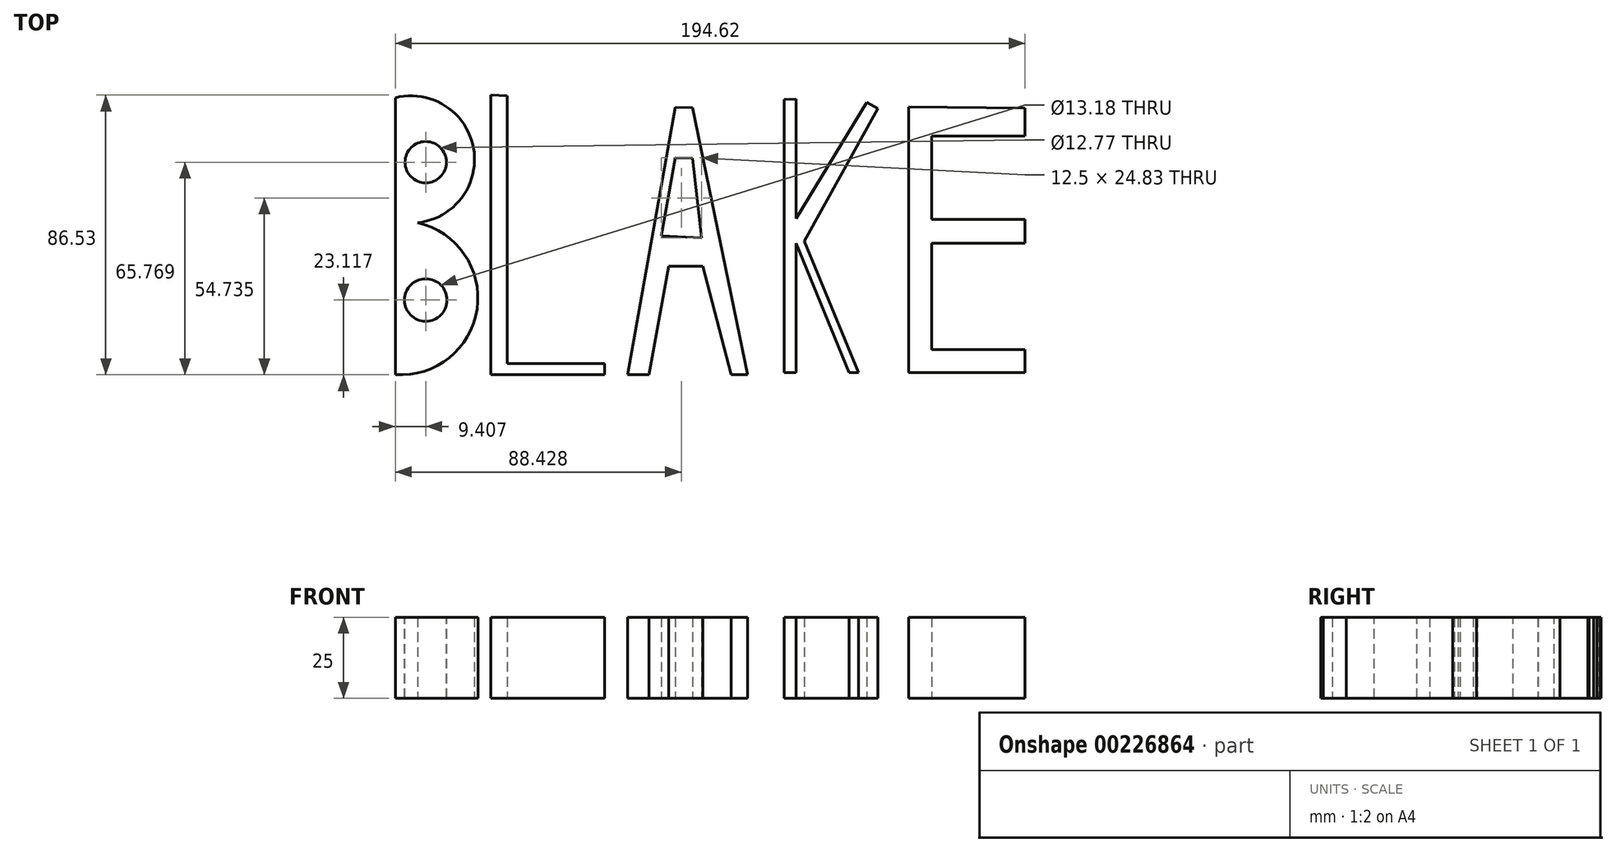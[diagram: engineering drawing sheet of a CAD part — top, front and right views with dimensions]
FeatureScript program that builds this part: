
annotation { "Feature Type Name" : "Feature", "Feature Type Description" : "" }
export const myFeature = defineFeature(function(context is Context, id is Id, definition is map)
    precondition{}
    {
        {
            var Q0;
            Q0=qCreatedBy(makeId("Top.planeOp"),FACE);
            var sketch = newSketch(context, id + "F0", { "sketchPlane" : qUnion([Q0])});
            skLineSegment(sketch, "E0", {"start": v(-86.48, 42.75) * mm, "end": v(-86.48, -42.9) * mm});
            skArc(sketch, "E1", {"start": v(-86.48, 4.57) * mm, "mid": v(-61.98, 23.66) * mm, "end": v(-86.48, 42.75) * mm});
            skArc(sketch, "E2", {"start": v(-86.48, -42.9) * mm, "mid": v(-60.94, -19.17) * mm, "end": v(-86.48, 4.57) * mm});
            skLineSegment(sketch, "E3", {"start": v(-56.92, 43.57) * mm, "end": v(-56.92, -42.88) * mm});
            skLineSegment(sketch, "E4", {"start": v(-56.92, -42.88) * mm, "end": v(-21.72, -42.88) * mm});
            skLineSegment(sketch, "E5", {"start": v(-21.72, -42.88) * mm, "end": v(-21.72, -39.43) * mm});
            skLineSegment(sketch, "E6", {"start": v(-21.72, -39.43) * mm, "end": v(-51.92, -39.43) * mm});
            skLineSegment(sketch, "E7", {"start": v(-51.92, -39.43) * mm, "end": v(-51.92, 43.4) * mm});
            skLineSegment(sketch, "E8", {"start": v(-51.92, 43.4) * mm, "end": v(-56.92, 43.57) * mm});
            skLineSegment(sketch, "E9", {"start": v(0, 39.78) * mm, "end": v(-14.7, -42.88) * mm});
            skLineSegment(sketch, "E10", {"start": v(-14.7, -42.88) * mm, "end": v(-8.02, -42.87) * mm});
            skLineSegment(sketch, "E11", {"start": v(-8.02, -42.87) * mm, "end": v(-2.03, -9.4) * mm});
            skLineSegment(sketch, "E12", {"start": v(-2.03, -9.4) * mm, "end": v(8.6, -9.4) * mm});
            skLineSegment(sketch, "E13", {"start": v(8.6, -9.4) * mm, "end": v(17.33, -42.88) * mm});
            skLineSegment(sketch, "E14", {"start": v(17.33, -42.88) * mm, "end": v(22.47, -42.88) * mm});
            skLineSegment(sketch, "E15", {"start": v(22.47, -42.88) * mm, "end": v(5.34, 39.6) * mm});
            skLineSegment(sketch, "E16", {"start": v(5.34, 39.6) * mm, "end": v(0, 39.78) * mm});
            skLineSegment(sketch, "E17", {"start": v(0, 24.19) * mm, "end": v(-4.3, 0) * mm});
            skLineSegment(sketch, "E18", {"start": v(-4.3, 0) * mm, "end": v(8.2, -0.64) * mm});
            skLineSegment(sketch, "E19", {"start": v(8.2, -0.64) * mm, "end": v(5.34, 24.02) * mm});
            skLineSegment(sketch, "E20", {"start": v(5.34, 24.02) * mm, "end": v(0, 24.19) * mm});
            skLineSegment(sketch, "E21", {"start": v(33.78, 42.18) * mm, "end": v(33.78, -42.29) * mm});
            skLineSegment(sketch, "E22", {"start": v(33.78, -42.29) * mm, "end": v(37.38, -42.29) * mm});
            skLineSegment(sketch, "E23", {"start": v(37.38, -42.29) * mm, "end": v(37.38, -2.2) * mm});
            skLineSegment(sketch, "E24", {"start": v(37.38, -2.2) * mm, "end": v(53.82, -42.29) * mm});
            skLineSegment(sketch, "E25", {"start": v(53.82, -42.29) * mm, "end": v(56.74, -42.29) * mm});
            skLineSegment(sketch, "E26", {"start": v(56.74, -42.29) * mm, "end": v(39.95, -1.68) * mm});
            skLineSegment(sketch, "E27", {"start": v(39.95, -1.68) * mm, "end": v(62.73, 39.44) * mm});
            skLineSegment(sketch, "E28", {"start": v(62.73, 39.44) * mm, "end": v(59.3, 41.34) * mm});
            skLineSegment(sketch, "E29", {"start": v(59.3, 41.34) * mm, "end": v(37.38, 5.34) * mm});
            skLineSegment(sketch, "E30", {"start": v(37.38, 5.34) * mm, "end": v(37.38, 42.35) * mm});
            skLineSegment(sketch, "E31", {"start": v(37.38, 42.35) * mm, "end": v(33.78, 42.18) * mm});
            skLineSegment(sketch, "E32", {"start": v(72.16, 39.93) * mm, "end": v(72.16, -42.29) * mm});
            skLineSegment(sketch, "E33", {"start": v(72.16, -42.29) * mm, "end": v(108.14, -42.29) * mm});
            skLineSegment(sketch, "E34", {"start": v(108.14, -42.29) * mm, "end": v(108.14, -35.1) * mm});
            skLineSegment(sketch, "E35", {"start": v(108.14, -35.1) * mm, "end": v(79.35, -35.1) * mm});
            skLineSegment(sketch, "E36", {"start": v(79.35, -35.1) * mm, "end": v(79.35, -2.21) * mm});
            skLineSegment(sketch, "E37", {"start": v(79.35, -2.21) * mm, "end": v(108.14, -2.21) * mm});
            skLineSegment(sketch, "E38", {"start": v(108.14, -2.21) * mm, "end": v(108.14, 5.15) * mm});
            skLineSegment(sketch, "E39", {"start": v(108.14, 5.15) * mm, "end": v(79.35, 5.15) * mm});
            skLineSegment(sketch, "E40", {"start": v(79.35, 5.15) * mm, "end": v(79.35, 30.85) * mm});
            skLineSegment(sketch, "E41", {"start": v(79.35, 30.85) * mm, "end": v(108.14, 30.85) * mm});
            skLineSegment(sketch, "E42", {"start": v(108.14, 30.85) * mm, "end": v(108.14, 39.59) * mm});
            skLineSegment(sketch, "E43", {"start": v(108.14, 39.59) * mm, "end": v(72.16, 39.93) * mm});
            skSolve(sketch);
        }
        {
            var Q0;
            Q0=makeQuery(id+"F0.imprint","IMPRINT",FACE,{"disambiguationData":[TD([[makeQuery(id+"F0.imprint","IMPRINT",EDGE,{"derivedFrom":sQuery(id+"F0.wireOp",EDGE,"E3")}),1.0]])]});
            var Q1;
            Q1=makeQuery(id+"F0.imprint","IMPRINT",FACE,{"disambiguationData":[TD([[makeQuery(id+"F0.imprint","IMPRINT",EDGE,{"derivedFrom":sQuery(id+"F0.wireOp",EDGE,"E21")}),1.0]])]});
            var Q2;
            Q2=makeQuery(id+"F0.imprint","IMPRINT",FACE,{"disambiguationData":[TD([[makeQuery(id+"F0.imprint","IMPRINT",EDGE,{"derivedFrom":sQuery(id+"F0.wireOp",EDGE,"E32")}),1.0]])]});
            var Q3;
            {var subQ0=sQuery(id+"F0.wireOp",EDGE,"E2");var subQ1=sQuery(id+"F0.wireOp",EDGE,"E0");var subQ2=makeQuery(id+"F0.imprint","INTERSECT",VERTEX,{"derivedFrom":[subQ1,subQ0]});Q3=makeQuery(id+"F0.imprint","IMPRINT",FACE,{"disambiguationData":[TD([[makeQuery(id+"F0.imprint","IMPRINT",EDGE,{"disambiguationData":[TD([[subQ2,-1.0]])],"derivedFrom":subQ0}),1.0]])]});}
            var Q4;
            Q4=makeQuery(id+"F0.imprint","IMPRINT",FACE,{"disambiguationData":[TD([[makeQuery(id+"F0.imprint","IMPRINT",EDGE,{"derivedFrom":sQuery(id+"F0.wireOp",EDGE,"E9")}),1.0]])]});
            var Q5;
            {var subQ0=sQuery(id+"F0.wireOp",EDGE,"E2");var subQ1=sQuery(id+"F0.wireOp",EDGE,"E1");var subQ3=makeQuery(id+"F0.imprint","INTERSECT",VERTEX,{"derivedFrom":[subQ1,subQ0]});Q5=makeQuery(id+"F0.imprint","IMPRINT",FACE,{"disambiguationData":[TD([[makeQuery(id+"F0.imprint","IMPRINT",EDGE,{"disambiguationData":[TD([[subQ3,1.0]])],"derivedFrom":subQ1}),1.0]])]});}
            var Q6;
            {var subQ0=sQuery(id+"F0.wireOp",EDGE,"E1");var subQ1=sQuery(id+"F0.wireOp",EDGE,"E0");var subQ2=makeQuery(id+"F0.imprint","INTERSECT",VERTEX,{"derivedFrom":[subQ1,subQ0]});Q6=makeQuery(id+"F0.imprint","IMPRINT",FACE,{"disambiguationData":[TD([[makeQuery(id+"F0.imprint","IMPRINT",EDGE,{"disambiguationData":[TD([[subQ2,1.0]])],"derivedFrom":subQ0}),1.0]])]});}
            extrude(context, id + "F1", {"entities" : qUnion([Q0, Q1, Q2, Q3, Q4, Q5, Q6]), "depth" : 25 * mm});
        }
        {
            var Q0;
            Q0=makeQuery(id+"F1.opExtrude","CAP_FACE",FACE,{"disambiguationData":[OSD([sQuery(id+"F0.wireOp",EDGE,"E0"),sQuery(id+"F0.wireOp",EDGE,"E1"),sQuery(id+"F0.wireOp",EDGE,"E2")])],"isStart":false});
            var sketch = newSketch(context, id + "F2", { "sketchPlane" : qUnion([Q0])});
            skCircle(sketch, "E44", {"center": v(-77.07, 22.8) * mm, "radius": 6.38 * mm});
            skCircle(sketch, "E45", {"center": v(-77.07, -19.84) * mm, "radius": 6.6 * mm});
            skSolve(sketch);
        }
        {
            var Q0;
            Q0=makeQuery(id+"F2.imprint","IMPRINT",FACE,{"disambiguationData":[TD([[makeQuery(id+"F2.imprint","IMPRINT",EDGE,{"derivedFrom":sQuery(id+"F2.wireOp",EDGE,"E44")}),1.0]])]});
            var Q1;
            Q1=makeQuery(id+"F2.imprint","IMPRINT",FACE,{"disambiguationData":[TD([[makeQuery(id+"F2.imprint","IMPRINT",EDGE,{"derivedFrom":sQuery(id+"F2.wireOp",EDGE,"E45")}),1.0]])]});
            extrude(context, id + "F3", {"entities" : qUnion([Q0, Q1]), "operationType" : NewBodyOperationType.REMOVE, "oppositeDirection" : true, "depth" : 35.6 * mm});
        }
    });
